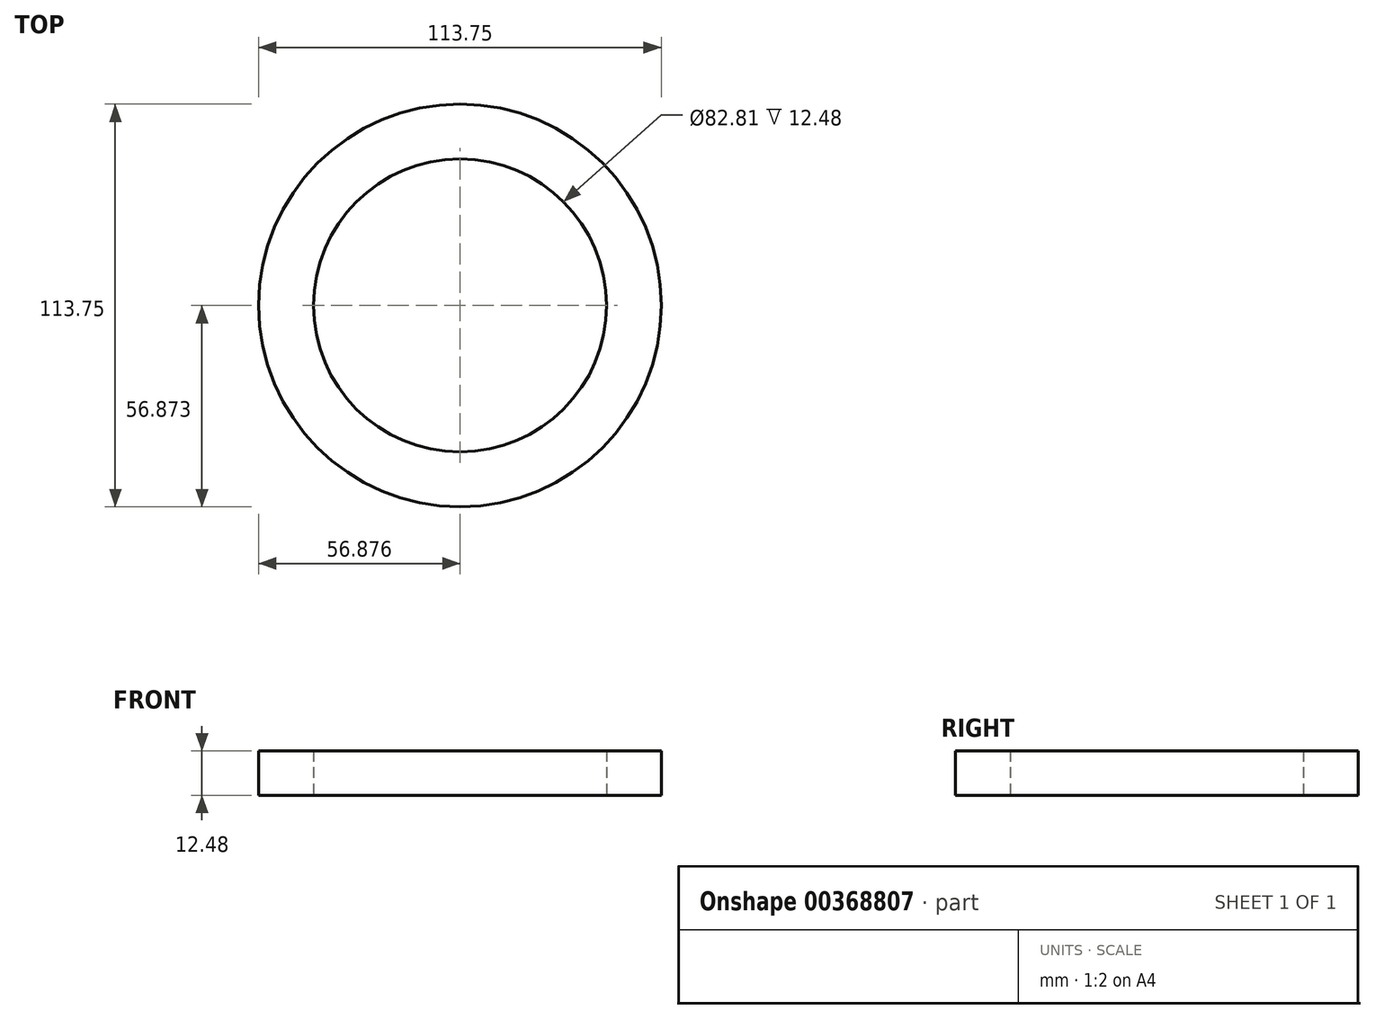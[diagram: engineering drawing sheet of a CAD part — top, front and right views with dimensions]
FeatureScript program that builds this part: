
annotation { "Feature Type Name" : "Feature", "Feature Type Description" : "" }
export const myFeature = defineFeature(function(context is Context, id is Id, definition is map)
    precondition{}
    {
        {
            var Q0;
            Q0=qCreatedBy(makeId("Top.planeOp"),FACE);
            var sketch = newSketch(context, id + "F0", { "sketchPlane" : qUnion([Q0])});
            skCircle(sketch, "E0", {"center": v(32.7, 18.55) * mm, "radius": 56.88 * mm});
            skCircle(sketch, "E1", {"center": v(32.7, 18.55) * mm, "radius": 41.4 * mm});
            skSolve(sketch);
        }
        {
            var Q0;
            Q0=makeQuery(id+"F0.imprint","IMPRINT",FACE,{"disambiguationData":[TD([[makeQuery(id+"F0.imprint","IMPRINT",EDGE,{"derivedFrom":sQuery(id+"F0.wireOp",EDGE,"E0")}),1.0]])]});
            extrude(context, id + "F1", {"entities" : qUnion([Q0]), "depth" : 12.48 * mm});
        }
    });
